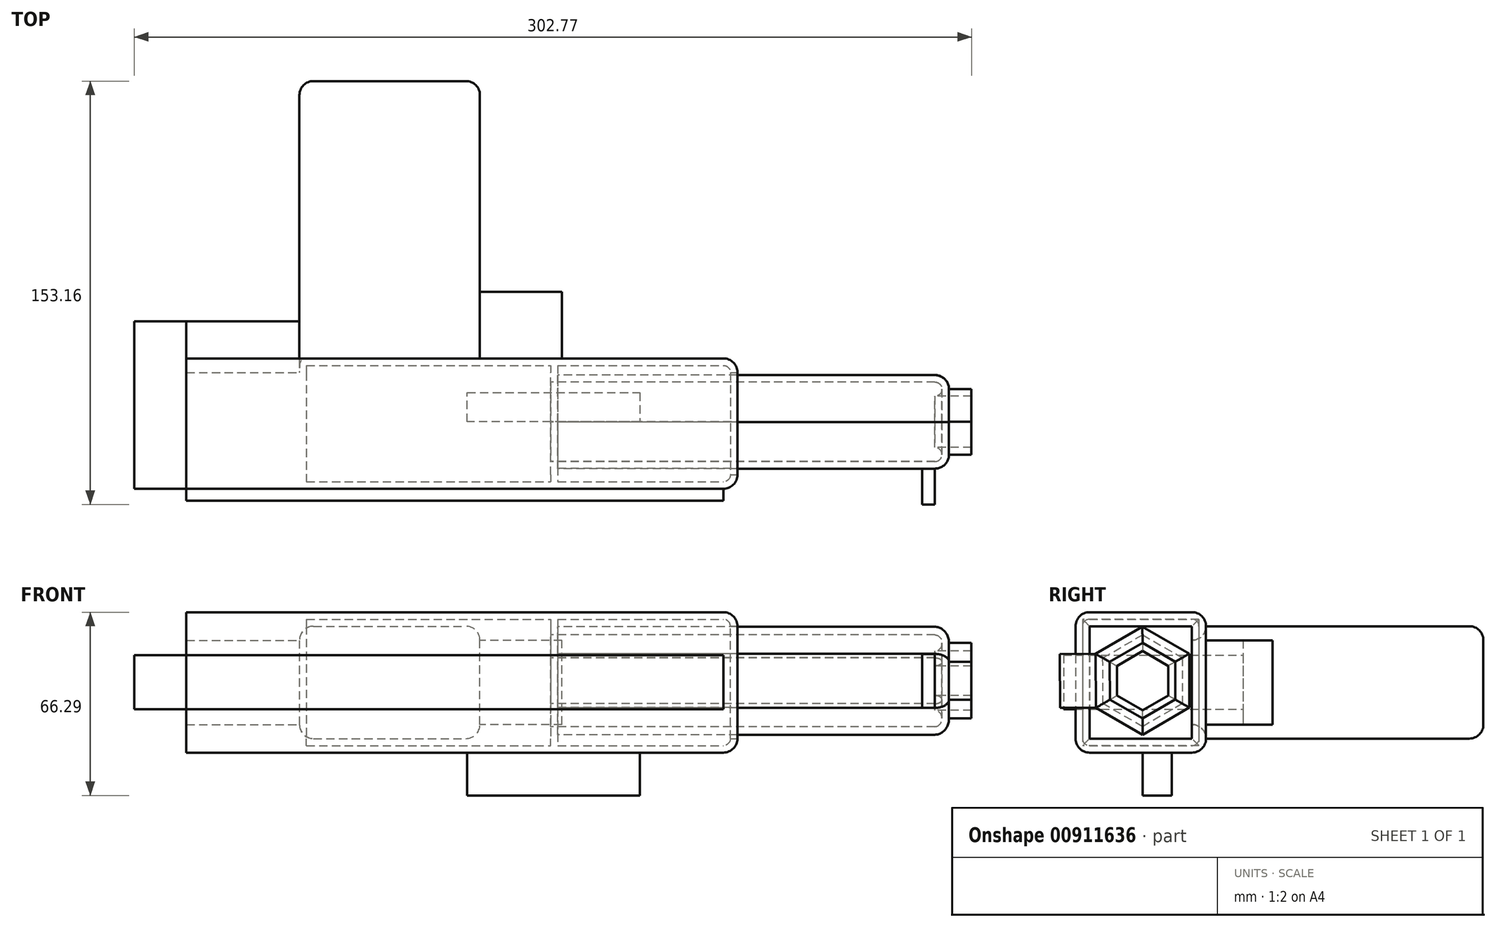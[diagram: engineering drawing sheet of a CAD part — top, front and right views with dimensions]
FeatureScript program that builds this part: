
annotation { "Feature Type Name" : "Feature", "Feature Type Description" : "" }
export const myFeature = defineFeature(function(context is Context, id is Id, definition is map)
    precondition{}
    {
        {
            var Q0;
            Q0=qCreatedBy(makeId("Top.planeOp"),FACE);
            var sketch = newSketch(context, id + "F0", { "sketchPlane" : qUnion([Q0])});
            skLineSegment(sketch, "E0.bottom", {"start": v(-32.17, 22.95) * mm, "end": v(35.3, 22.95) * mm});
            skLineSegment(sketch, "E0.top", {"start": v(-32.17, -24.24) * mm, "end": v(35.3, -24.24) * mm});
            skLineSegment(sketch, "E0.left", {"start": v(-32.17, 22.95) * mm, "end": v(-32.17, -24.24) * mm});
            skLineSegment(sketch, "E0.right", {"start": v(35.3, 22.95) * mm, "end": v(35.3, -24.24) * mm});
            skSolve(sketch);
        }
        {
            var Q0;
            Q0=makeQuery(id+"F0.imprint","IMPRINT",FACE,{"disambiguationData":[TD([[makeQuery(id+"F0.imprint","IMPRINT",EDGE,{"derivedFrom":sQuery(id+"F0.wireOp",EDGE,"E0.bottom")}),-1.0]])]});
            extrude(context, id + "F1", {"entities" : qUnion([Q0]), "depth" : 50.8 * mm, "offsetDistance" : 25.4 * mm});
        }
        {
            var Q0;
            Q0=makeQuery(id+"F1.opExtrude","CAP_EDGE",EDGE,{"disambiguationData":[OSD([sQuery(id+"F0.wireOp",EDGE,"E0.right")])],"isStart":false});
            var Q1;
            Q1=makeQuery(id+"F1.opExtrude","SWEPT_EDGE",EDGE,{"disambiguationData":[OSD([sQuery(id+"F0.wireOp",EDGE,"E0.top"),sQuery(id+"F0.wireOp",EDGE,"E0.right")])]});
            var Q2;
            Q2=makeQuery(id+"F1.opExtrude","CAP_EDGE",EDGE,{"disambiguationData":[OSD([sQuery(id+"F0.wireOp",EDGE,"E0.right")])],"isStart":true});
            var Q3;
            Q3=makeQuery(id+"F1.opExtrude","SWEPT_EDGE",EDGE,{"disambiguationData":[OSD([sQuery(id+"F0.wireOp",EDGE,"E0.bottom"),sQuery(id+"F0.wireOp",EDGE,"E0.right")])]});
            fillet(context, id + "F2", {"entities" : qUnion([Q0, Q1, Q2, Q3]), "radius" : 5.08 * mm, "tangentPropagation" : true, "allowEdgeOverflow" : false});
        }
        {
            var Q0;
            Q0=makeQuery(id+"F1.opExtrude","SWEPT_FACE",FACE,{"disambiguationData":[OSD([sQuery(id+"F0.wireOp",EDGE,"E0.right")])]});
            shell(context, id + "F3", {"entities" : qUnion([Q0]), "thickness" : 2.54 * mm});
        }
        {
            var Q0;
            Q0=makeQuery(id+"F1.opExtrude","CAP_EDGE",EDGE,{"disambiguationData":[OSD([sQuery(id+"F0.wireOp",EDGE,"E0.top")])],"isStart":true});
            var Q1;
            Q1=makeQuery(id+"F1.opExtrude","CAP_EDGE",EDGE,{"disambiguationData":[OSD([sQuery(id+"F0.wireOp",EDGE,"E0.bottom")])],"isStart":true});
            var Q2;
            Q2=makeQuery(id+"F1.opExtrude","CAP_EDGE",EDGE,{"disambiguationData":[OSD([sQuery(id+"F0.wireOp",EDGE,"E0.bottom")])],"isStart":false});
            var Q3;
            Q3=makeQuery(id+"F1.opExtrude","CAP_EDGE",EDGE,{"disambiguationData":[OSD([sQuery(id+"F0.wireOp",EDGE,"E0.top")])],"isStart":false});
            fillet(context, id + "F4", {"entities" : qUnion([Q0, Q1, Q2, Q3]), "radius" : 5.08 * mm, "tangentPropagation" : true, "allowEdgeOverflow" : false});
        }
        {
            var Q0;
            Q0=makeQuery(id+"F3.opShell","OFFSET_FACE",FACE,{"disambiguationData":[OSD([sQuery(id+"F0.wireOp",EDGE,"E0.left")])]});
            var sketch = newSketch(context, id + "F5", { "sketchPlane" : qUnion([Q0])});
            skCircle(sketch, "E1.cCircle", {"center": v(0, 26) * mm, "radius": 16.9 * mm, "construction": true});
            skLineSegment(sketch, "E1.0", {"start": v(-16.93, 35.73) * mm, "end": v(-0.04, 45.53) * mm});
            skLineSegment(sketch, "E1.1", {"start": v(-0.04, 45.53) * mm, "end": v(16.89, 35.8) * mm});
            skLineSegment(sketch, "E1.2", {"start": v(16.89, 35.8) * mm, "end": v(16.93, 16.28) * mm});
            skLineSegment(sketch, "E1.3", {"start": v(16.93, 16.28) * mm, "end": v(0.04, 6.48) * mm});
            skLineSegment(sketch, "E1.4", {"start": v(0.04, 6.48) * mm, "end": v(-16.89, 16.2) * mm});
            skLineSegment(sketch, "E1.5", {"start": v(-16.89, 16.2) * mm, "end": v(-16.93, 35.73) * mm});
            skPoint(sketch, "E1.0.midPoint", {"position": v(-8.48, 40.63) * mm});
            skSolve(sketch);
        }
        {
            var Q0;
            Q0 = qSketchRegion(id + "F5", true);
            extrude(context, id + "F6", {"entities" : qUnion([Q0]), "operationType" : NewBodyOperationType.ADD, "depth" : 141.48 * mm, "offsetDistance" : 25.4 * mm});
        }
        {
            var Q0;
            Q0=makeQuery(id+"F6.opExtrude","CAP_EDGE",EDGE,{"disambiguationData":[OSD([sQuery(id+"F5.wireOp",EDGE,"E1.5")])],"isStart":false});
            var Q1;
            Q1=makeQuery(id+"F6.opExtrude","CAP_EDGE",EDGE,{"disambiguationData":[OSD([sQuery(id+"F5.wireOp",EDGE,"E1.2")])],"isStart":false});
            var Q2;
            Q2=makeQuery(id+"F6.opExtrude","CAP_EDGE",EDGE,{"disambiguationData":[OSD([sQuery(id+"F5.wireOp",EDGE,"E1.4")])],"isStart":false});
            var Q3;
            Q3=makeQuery(id+"F6.opExtrude","CAP_EDGE",EDGE,{"disambiguationData":[OSD([sQuery(id+"F5.wireOp",EDGE,"E1.0")])],"isStart":false});
            var Q4;
            Q4=makeQuery(id+"F6.opExtrude","CAP_EDGE",EDGE,{"disambiguationData":[OSD([sQuery(id+"F5.wireOp",EDGE,"E1.1")])],"isStart":false});
            var Q5;
            Q5=makeQuery(id+"F6.opExtrude","CAP_EDGE",EDGE,{"disambiguationData":[OSD([sQuery(id+"F5.wireOp",EDGE,"E1.3")])],"isStart":false});
            fillet(context, id + "F7", {"entities" : qUnion([Q0, Q1, Q2, Q3, Q4, Q5]), "radius" : 5.08 * mm, "tangentPropagation" : true, "allowEdgeOverflow" : false});
        }
        {
            var Q0;
            Q0=makeQuery(id+"F6.opExtrude","CAP_FACE",FACE,{"disambiguationData":[OSD([sQuery(id+"F5.wireOp",EDGE,"E1.0"),sQuery(id+"F5.wireOp",EDGE,"E1.1"),sQuery(id+"F5.wireOp",EDGE,"E1.2"),sQuery(id+"F5.wireOp",EDGE,"E1.3"),sQuery(id+"F5.wireOp",EDGE,"E1.4"),sQuery(id+"F5.wireOp",EDGE,"E1.5")])],"isStart":false});
            extrude(context, id + "F8", {"entities" : qUnion([Q0]), "operationType" : NewBodyOperationType.ADD, "depth" : 8.13 * mm, "offsetDistance" : 25.4 * mm});
        }
        {
            var Q0;
            Q0=makeQuery(id+"F1.opExtrude","SWEPT_FACE",FACE,{"disambiguationData":[OSD([sQuery(id+"F0.wireOp",EDGE,"E0.left")])]});
            extrude(context, id + "F9", {"entities" : qUnion([Q0]), "operationType" : NewBodyOperationType.ADD, "depth" : 90.93 * mm, "offsetDistance" : 25.4 * mm});
        }
        {
            var Q0;
            Q0=makeQuery(id+"F8.opExtrude","CAP_FACE",FACE,{"disambiguationData":[OSD([sQuery(id+"F5.wireOp",EDGE,"E1.0"),sQuery(id+"F5.wireOp",EDGE,"E1.1"),sQuery(id+"F5.wireOp",EDGE,"E1.2"),sQuery(id+"F5.wireOp",EDGE,"E1.3"),sQuery(id+"F5.wireOp",EDGE,"E1.4"),sQuery(id+"F5.wireOp",EDGE,"E1.5")])],"isStart":false});
            shell(context, id + "F10", {"entities" : qUnion([Q0]), "thickness" : 2.54 * mm});
        }
        {
            var Q0;
            {var subQ0=sQuery(id+"F0.wireOp",EDGE,"E0.left");var subQ1=sQuery(id+"F0.wireOp",EDGE,"E0.bottom");Q0=makeQuery(id+"F9.boolean.opBoolean","MERGE",FACE,{"derivedFrom":[makeQuery(id+"F1.opExtrude","SWEPT_FACE",FACE,{"disambiguationData":[OSD([subQ1])]}),makeQuery(id+"F9.opExtrude","SWEPT_FACE",FACE,{"disambiguationData":[OSD([subQ1,subQ0]),TDD([makeQuery(id+"F1.opExtrude","SWEPT_EDGE",EDGE,{"disambiguationData":[OSD([subQ1,subQ0])]})])]})]});}
            var sketch = newSketch(context, id + "F11", { "sketchPlane" : qUnion([Q0])});
            skLineSegment(sketch, "E2", {"start": v(57.84, 5.08) * mm, "end": v(57.84, 45.72) * mm});
            skSolve(sketch);
        }
        {
            var Q0;
            {var subQ0=sQuery(id+"F11.wireOp",EDGE,"E2");Q0=makeQuery(id+"F11.imprint","IMPRINT",FACE,{"disambiguationData":[TD([[makeQuery(id+"F11.imprint","IMPRINT",EDGE,{"derivedFrom":subQ0}),-1.0]])]});}
            extrude(context, id + "F12", {"entities" : qUnion([Q0]), "operationType" : NewBodyOperationType.ADD, "depth" : 100.33 * mm, "offsetDistance" : 25.4 * mm});
        }
        {
            var Q0;
            {var subQ0=sQuery(id+"F11.wireOp",EDGE,"E2");var subQ1=sQuery(id+"F0.wireOp",EDGE,"E0.bottom");var subQ2=makeQuery(id+"F1.opExtrude","SWEPT_FACE",FACE,{"disambiguationData":[OSD([subQ1])]});var subQ3=sQuery(id+"F0.wireOp",EDGE,"E0.left");var subQ4=makeQuery(id+"F1.opExtrude","CAP_EDGE",EDGE,{"disambiguationData":[OSD([subQ1])],"isStart":true});Q0=makeQuery(id+"F12.opExtrude","SWEPT_EDGE",EDGE,{"disambiguationData":[OSD([subQ1,subQ3,subQ0]),TDD([makeQuery(id+"F11.imprint","INTERSECT",VERTEX,{"derivedFrom":[makeQuery(id+"F9.boolean.opBoolean","MERGE",EDGE,{"derivedFrom":[makeQuery(id+"F4.opFillet","BLEND_EDGE",EDGE,{"blendedFrom":[subQ4,subQ2],"blendedInto":[subQ2]}),makeQuery(id+"F9.opExtrude","SWEPT_EDGE",EDGE,{"disambiguationData":[OSD([subQ1,subQ3]),TDD([makeQuery(id+"F4.opFillet","BLEND_VERTEX",VERTEX,{"blendedFrom":[subQ4,makeQuery(id+"F1.opExtrude","SWEPT_FACE",FACE,{"disambiguationData":[OSD([subQ3])]}),subQ2],"blendedInto":[makeQuery(id+"F1.opExtrude","SWEPT_FACE",FACE,{"disambiguationData":[OSD([subQ3])]}),subQ2]})])]})]}),subQ0]})])]});}
            var Q1;
            {var subQ0=sQuery(id+"F11.wireOp",EDGE,"E2");var subQ1=sQuery(id+"F0.wireOp",EDGE,"E0.bottom");var subQ2=makeQuery(id+"F1.opExtrude","SWEPT_FACE",FACE,{"disambiguationData":[OSD([subQ1])]});var subQ3=sQuery(id+"F0.wireOp",EDGE,"E0.left");var subQ4=makeQuery(id+"F1.opExtrude","CAP_EDGE",EDGE,{"disambiguationData":[OSD([subQ1])],"isStart":false});Q1=makeQuery(id+"F12.opExtrude","SWEPT_EDGE",EDGE,{"disambiguationData":[OSD([subQ1,subQ3,subQ0]),TDD([makeQuery(id+"F11.imprint","INTERSECT",VERTEX,{"derivedFrom":[makeQuery(id+"F9.boolean.opBoolean","MERGE",EDGE,{"derivedFrom":[makeQuery(id+"F4.opFillet","BLEND_EDGE",EDGE,{"blendedFrom":[subQ4,subQ2],"blendedInto":[subQ2]}),makeQuery(id+"F9.opExtrude","SWEPT_EDGE",EDGE,{"disambiguationData":[OSD([subQ1,subQ3]),TDD([makeQuery(id+"F4.opFillet","BLEND_VERTEX",VERTEX,{"blendedFrom":[subQ4,makeQuery(id+"F1.opExtrude","SWEPT_FACE",FACE,{"disambiguationData":[OSD([subQ3])]}),subQ2],"blendedInto":[makeQuery(id+"F1.opExtrude","SWEPT_FACE",FACE,{"disambiguationData":[OSD([subQ3])]}),subQ2]})])]})]}),subQ0]})])]});}
            var Q2;
            {var subQ0=sQuery(id+"F0.wireOp",EDGE,"E0.bottom");var subQ1=makeQuery(id+"F1.opExtrude","SWEPT_FACE",FACE,{"disambiguationData":[OSD([subQ0])]});var subQ2=sQuery(id+"F0.wireOp",EDGE,"E0.left");var subQ3=makeQuery(id+"F1.opExtrude","CAP_EDGE",EDGE,{"disambiguationData":[OSD([subQ0])],"isStart":false});Q2=makeQuery(id+"F12.opExtrude","SWEPT_EDGE",EDGE,{"disambiguationData":[OSD([subQ0,subQ2]),TDD([makeQuery(id+"F11.imprint","INTERSECT",VERTEX,{"derivedFrom":[makeQuery(id+"F9.opExtrude","CAP_EDGE",EDGE,{"disambiguationData":[OSD([subQ0,subQ2]),TDD([makeQuery(id+"F1.opExtrude","SWEPT_EDGE",EDGE,{"disambiguationData":[OSD([subQ0,subQ2])]})])],"isStart":false}),makeQuery(id+"F9.boolean.opBoolean","MERGE",EDGE,{"derivedFrom":[makeQuery(id+"F4.opFillet","BLEND_EDGE",EDGE,{"blendedFrom":[subQ3,subQ1],"blendedInto":[subQ1]}),makeQuery(id+"F9.opExtrude","SWEPT_EDGE",EDGE,{"disambiguationData":[OSD([subQ0,subQ2]),TDD([makeQuery(id+"F4.opFillet","BLEND_VERTEX",VERTEX,{"blendedFrom":[subQ3,makeQuery(id+"F1.opExtrude","SWEPT_FACE",FACE,{"disambiguationData":[OSD([subQ2])]}),subQ1],"blendedInto":[makeQuery(id+"F1.opExtrude","SWEPT_FACE",FACE,{"disambiguationData":[OSD([subQ2])]}),subQ1]})])]})]})]})])]});}
            var Q3;
            {var subQ0=sQuery(id+"F0.wireOp",EDGE,"E0.bottom");var subQ1=makeQuery(id+"F1.opExtrude","SWEPT_FACE",FACE,{"disambiguationData":[OSD([subQ0])]});var subQ2=sQuery(id+"F0.wireOp",EDGE,"E0.left");var subQ3=makeQuery(id+"F1.opExtrude","CAP_EDGE",EDGE,{"disambiguationData":[OSD([subQ0])],"isStart":true});Q3=makeQuery(id+"F12.opExtrude","SWEPT_EDGE",EDGE,{"disambiguationData":[OSD([subQ0,subQ2]),TDD([makeQuery(id+"F11.imprint","INTERSECT",VERTEX,{"derivedFrom":[makeQuery(id+"F9.opExtrude","CAP_EDGE",EDGE,{"disambiguationData":[OSD([subQ0,subQ2]),TDD([makeQuery(id+"F1.opExtrude","SWEPT_EDGE",EDGE,{"disambiguationData":[OSD([subQ0,subQ2])]})])],"isStart":false}),makeQuery(id+"F9.boolean.opBoolean","MERGE",EDGE,{"derivedFrom":[makeQuery(id+"F4.opFillet","BLEND_EDGE",EDGE,{"blendedFrom":[subQ3,subQ1],"blendedInto":[subQ1]}),makeQuery(id+"F9.opExtrude","SWEPT_EDGE",EDGE,{"disambiguationData":[OSD([subQ0,subQ2]),TDD([makeQuery(id+"F4.opFillet","BLEND_VERTEX",VERTEX,{"blendedFrom":[subQ3,makeQuery(id+"F1.opExtrude","SWEPT_FACE",FACE,{"disambiguationData":[OSD([subQ2])]}),subQ1],"blendedInto":[makeQuery(id+"F1.opExtrude","SWEPT_FACE",FACE,{"disambiguationData":[OSD([subQ2])]}),subQ1]})])]})]})]})])]});}
            var Q4;
            {var subQ0=sQuery(id+"F0.wireOp",EDGE,"E0.bottom");var subQ1=makeQuery(id+"F1.opExtrude","SWEPT_FACE",FACE,{"disambiguationData":[OSD([subQ0])]});var subQ2=sQuery(id+"F0.wireOp",EDGE,"E0.left");var subQ3=makeQuery(id+"F1.opExtrude","CAP_EDGE",EDGE,{"disambiguationData":[OSD([subQ0])],"isStart":true});var subQ4=makeQuery(id+"F9.boolean.opBoolean","MERGE",EDGE,{"derivedFrom":[makeQuery(id+"F4.opFillet","BLEND_EDGE",EDGE,{"blendedFrom":[subQ3,subQ1],"blendedInto":[subQ1]}),makeQuery(id+"F9.opExtrude","SWEPT_EDGE",EDGE,{"disambiguationData":[OSD([subQ0,subQ2]),TDD([makeQuery(id+"F4.opFillet","BLEND_VERTEX",VERTEX,{"blendedFrom":[subQ3,makeQuery(id+"F1.opExtrude","SWEPT_FACE",FACE,{"disambiguationData":[OSD([subQ2])]}),subQ1],"blendedInto":[makeQuery(id+"F1.opExtrude","SWEPT_FACE",FACE,{"disambiguationData":[OSD([subQ2])]}),subQ1]})])]})]});Q4=makeQuery(id+"F12.opExtrude","CAP_EDGE",EDGE,{"disambiguationData":[OSD([subQ0,subQ2]),TDD([makeQuery(id+"F11.imprint","IMPRINT",EDGE,{"disambiguationData":[TD([[makeQuery(id+"F11.imprint","INTERSECT",VERTEX,{"derivedFrom":[subQ4,sQuery(id+"F11.wireOp",EDGE,"E2")]}),-1.0]])],"derivedFrom":subQ4})])],"isStart":false});}
            var Q5;
            {var subQ0=sQuery(id+"F0.wireOp",EDGE,"E0.bottom");var subQ1=makeQuery(id+"F1.opExtrude","SWEPT_FACE",FACE,{"disambiguationData":[OSD([subQ0])]});var subQ2=sQuery(id+"F0.wireOp",EDGE,"E0.left");var subQ3=makeQuery(id+"F1.opExtrude","CAP_EDGE",EDGE,{"disambiguationData":[OSD([subQ0])],"isStart":false});var subQ4=makeQuery(id+"F9.boolean.opBoolean","MERGE",EDGE,{"derivedFrom":[makeQuery(id+"F4.opFillet","BLEND_EDGE",EDGE,{"blendedFrom":[subQ3,subQ1],"blendedInto":[subQ1]}),makeQuery(id+"F9.opExtrude","SWEPT_EDGE",EDGE,{"disambiguationData":[OSD([subQ0,subQ2]),TDD([makeQuery(id+"F4.opFillet","BLEND_VERTEX",VERTEX,{"blendedFrom":[subQ3,makeQuery(id+"F1.opExtrude","SWEPT_FACE",FACE,{"disambiguationData":[OSD([subQ2])]}),subQ1],"blendedInto":[makeQuery(id+"F1.opExtrude","SWEPT_FACE",FACE,{"disambiguationData":[OSD([subQ2])]}),subQ1]})])]})]});Q5=makeQuery(id+"F12.opExtrude","CAP_EDGE",EDGE,{"disambiguationData":[OSD([subQ0,subQ2]),TDD([makeQuery(id+"F11.imprint","IMPRINT",EDGE,{"disambiguationData":[TD([[makeQuery(id+"F11.imprint","INTERSECT",VERTEX,{"derivedFrom":[subQ4,sQuery(id+"F11.wireOp",EDGE,"E2")]}),1.0]])],"derivedFrom":subQ4})])],"isStart":false});}
            var Q6;
            {var subQ0=sQuery(id+"F0.wireOp",EDGE,"E0.left");var subQ1=sQuery(id+"F0.wireOp",EDGE,"E0.bottom");Q6=makeQuery(id+"F12.opExtrude","CAP_EDGE",EDGE,{"disambiguationData":[OSD([subQ1,subQ0]),TDD([makeQuery(id+"F11.imprint","IMPRINT",EDGE,{"derivedFrom":makeQuery(id+"F9.opExtrude","CAP_EDGE",EDGE,{"disambiguationData":[OSD([subQ1,subQ0]),TDD([makeQuery(id+"F1.opExtrude","SWEPT_EDGE",EDGE,{"disambiguationData":[OSD([subQ1,subQ0])]})])],"isStart":false})})])],"isStart":false});}
            var Q7;
            Q7=makeQuery(id+"F12.opExtrude","CAP_EDGE",EDGE,{"disambiguationData":[OSD([sQuery(id+"F11.wireOp",EDGE,"E2")])],"isStart":false});
            fillet(context, id + "F13", {"entities" : qUnion([Q0, Q1, Q2, Q3, Q4, Q5, Q6, Q7]), "radius" : 5.08 * mm, "tangentPropagation" : true, "allowEdgeOverflow" : false});
        }
        {
            var Q0;
            {var subQ0=sQuery(id+"F0.wireOp",EDGE,"E0.left");var subQ1=sQuery(id+"F0.wireOp",EDGE,"E0.bottom");Q0=makeQuery(id+"F12.boolean.opBoolean","MERGE",FACE,{"derivedFrom":[makeQuery(id+"F9.opExtrude","CAP_FACE",FACE,{"disambiguationData":[OSD([subQ0])],"isStart":false}),makeQuery(id+"F12.opExtrude","SWEPT_FACE",FACE,{"disambiguationData":[OSD([subQ1,subQ0]),TDD([makeQuery(id+"F11.imprint","IMPRINT",EDGE,{"derivedFrom":makeQuery(id+"F9.opExtrude","CAP_EDGE",EDGE,{"disambiguationData":[OSD([subQ1,subQ0]),TDD([makeQuery(id+"F1.opExtrude","SWEPT_EDGE",EDGE,{"disambiguationData":[OSD([subQ1,subQ0])]})])],"isStart":false})})])]})]});}
            var sketch = newSketch(context, id + "F14", { "sketchPlane" : qUnion([Q0])});
            skLineSegment(sketch, "E3", {"start": v(-17.87, 40.64) * mm, "end": v(-17.87, 10.16) * mm});
            skSolve(sketch);
        }
        {
            var Q0;
            Q0=makeQuery(id+"F14.imprint","IMPRINT",FACE,{"disambiguationData":[TD([[makeQuery(id+"F14.imprint","IMPRINT",EDGE,{"derivedFrom":sQuery(id+"F14.wireOp",EDGE,"E3")}),1.0]])]});
            extrude(context, id + "F15", {"entities" : qUnion([Q0]), "operationType" : NewBodyOperationType.ADD, "depth" : 40.9 * mm, "offsetDistance" : 25.4 * mm});
        }
        {
            var Q0;
            {var subQ0=sQuery(id+"F0.wireOp",EDGE,"E0.left");var subQ1=makeQuery(id+"F1.opExtrude","CAP_EDGE",EDGE,{"disambiguationData":[OSD([subQ0])],"isStart":true});Q0=makeQuery(id+"F15.boolean.opBoolean","MERGE",FACE,{"derivedFrom":[makeQuery(id+"F9.boolean.opBoolean","MERGE",FACE,{"derivedFrom":[makeQuery(id+"F1.opExtrude","CAP_FACE",FACE,{"disambiguationData":[OSD([sQuery(id+"F0.wireOp",EDGE,"E0.bottom"),sQuery(id+"F0.wireOp",EDGE,"E0.top"),subQ0,sQuery(id+"F0.wireOp",EDGE,"E0.right")])],"isStart":true}),makeQuery(id+"F9.opExtrude","SWEPT_FACE",FACE,{"disambiguationData":[OSD([subQ0]),TDD([subQ1])]})]}),makeQuery(id+"F15.opExtrude","SWEPT_FACE",FACE,{"disambiguationData":[OSD([subQ0]),TDD([makeQuery(id+"F14.imprint","IMPRINT",EDGE,{"derivedFrom":makeQuery(id+"F9.opExtrude","CAP_EDGE",EDGE,{"disambiguationData":[OSD([subQ0]),TDD([subQ1])],"isStart":false})})])]})]});}
            var sketch = newSketch(context, id + "F16", { "sketchPlane" : qUnion([Q0])});
            skLineSegment(sketch, "E4", {"start": v(0, 0) * mm, "end": v(-62.4, 0) * mm});
            skLineSegment(sketch, "E5", {"start": v(-62.4, 0) * mm, "end": v(-62.4, -10.55) * mm});
            skLineSegment(sketch, "E6", {"start": v(-62.4, -10.55) * mm, "end": v(0, -10.55) * mm});
            skLineSegment(sketch, "E7", {"start": v(0, -10.55) * mm, "end": v(0, 0) * mm});
            skSolve(sketch);
        }
        {
            var Q0;
            Q0=makeQuery(id+"F16.imprint","IMPRINT",FACE,{"disambiguationData":[TD([[makeQuery(id+"F16.imprint","IMPRINT",EDGE,{"derivedFrom":sQuery(id+"F16.wireOp",EDGE,"E4")}),1.0]])]});
            extrude(context, id + "F17", {"entities" : qUnion([Q0]), "operationType" : NewBodyOperationType.ADD, "depth" : 15.5 * mm, "offsetDistance" : 25.4 * mm});
        }
        {
            var Q0;
            Q0=makeQuery(id+"F15.opExtrude","CAP_FACE",FACE,{"disambiguationData":[OSD([sQuery(id+"F0.wireOp",EDGE,"E0.bottom"),sQuery(id+"F0.wireOp",EDGE,"E0.top"),sQuery(id+"F0.wireOp",EDGE,"E0.left"),sQuery(id+"F14.wireOp",EDGE,"E3")])],"isStart":false});
            var sketch = newSketch(context, id + "F18", { "sketchPlane" : qUnion([Q0])});
            skLineSegment(sketch, "E8", {"start": v(24.24, 35.3) * mm, "end": v(-17.87, 35.3) * mm});
            skLineSegment(sketch, "E9", {"start": v(24.24, 15.64) * mm, "end": v(-17.87, 15.64) * mm});
            skSolve(sketch);
        }
        {
            var Q0;
            {var subQ0=sQuery(id+"F18.wireOp",EDGE,"E8");Q0=makeQuery(id+"F18.imprint","IMPRINT",FACE,{"disambiguationData":[TD([[makeQuery(id+"F18.imprint","IMPRINT",EDGE,{"derivedFrom":subQ0}),1.0]])]});}
            extrude(context, id + "F19", {"entities" : qUnion([Q0]), "operationType" : NewBodyOperationType.ADD, "depth" : 18.8 * mm, "offsetDistance" : 25.4 * mm});
        }
        {
            var Q0;
            {var subQ0=sQuery(id+"F0.wireOp",EDGE,"E0.left");var subQ1=sQuery(id+"F0.wireOp",EDGE,"E0.top");var subQ2=makeQuery(id+"F1.opExtrude","SWEPT_EDGE",EDGE,{"disambiguationData":[OSD([subQ1,subQ0])]});Q0=makeQuery(id+"F19.boolean.opBoolean","MERGE",FACE,{"derivedFrom":[makeQuery(id+"F15.boolean.opBoolean","MERGE",FACE,{"derivedFrom":[makeQuery(id+"F9.boolean.opBoolean","MERGE",FACE,{"derivedFrom":[makeQuery(id+"F1.opExtrude","SWEPT_FACE",FACE,{"disambiguationData":[OSD([subQ1])]}),makeQuery(id+"F9.opExtrude","SWEPT_FACE",FACE,{"disambiguationData":[OSD([subQ1,subQ0]),TDD([subQ2])]})]}),makeQuery(id+"F15.opExtrude","SWEPT_FACE",FACE,{"disambiguationData":[OSD([subQ1,subQ0]),TDD([makeQuery(id+"F14.imprint","IMPRINT",EDGE,{"derivedFrom":makeQuery(id+"F9.opExtrude","CAP_EDGE",EDGE,{"disambiguationData":[OSD([subQ1,subQ0]),TDD([subQ2])],"isStart":false})})])]})]}),makeQuery(id+"F19.opExtrude","SWEPT_FACE",FACE,{"disambiguationData":[OSD([subQ1,subQ0])]})]});}
            var sketch = newSketch(context, id + "F20", { "sketchPlane" : qUnion([Q0])});
            skLineSegment(sketch, "E10", {"start": v(-164, 35.3) * mm, "end": v(30.22, 35.3) * mm});
            skLineSegment(sketch, "E11", {"start": v(-164, 15.64) * mm, "end": v(30.22, 15.64) * mm});
            skLineSegment(sketch, "E12", {"start": v(-164, 35.3) * mm, "end": v(-164, 15.64) * mm});
            skSolve(sketch);
        }
        {
            var Q0;
            {var subQ0=sQuery(id+"F20.wireOp",EDGE,"E10");Q0=makeQuery(id+"F20.imprint","IMPRINT",FACE,{"disambiguationData":[TD([[makeQuery(id+"F20.imprint","IMPRINT",EDGE,{"derivedFrom":subQ0}),-1.0]])]});}
            extrude(context, id + "F21", {"entities" : qUnion([Q0]), "operationType" : NewBodyOperationType.ADD, "depth" : 4.32 * mm, "offsetDistance" : 25.4 * mm});
        }
        {
            var Q0;
            Q0=makeQuery(id+"F12.opExtrude","SWEPT_FACE",FACE,{"disambiguationData":[OSD([sQuery(id+"F11.wireOp",EDGE,"E2")])]});
            var sketch = newSketch(context, id + "F22", { "sketchPlane" : qUnion([Q0])});
            skLineSegment(sketch, "E13", {"start": v(46.97, 10.16) * mm, "end": v(46.97, 40.64) * mm});
            skSolve(sketch);
        }
        {
            var Q0;
            {var subQ0=sQuery(id+"F22.wireOp",EDGE,"E13");Q0=makeQuery(id+"F22.imprint","IMPRINT",FACE,{"disambiguationData":[TD([[makeQuery(id+"F22.imprint","IMPRINT",EDGE,{"derivedFrom":subQ0}),1.0]])]});}
            extrude(context, id + "F23", {"entities" : qUnion([Q0]), "operationType" : NewBodyOperationType.ADD, "depth" : 29.72 * mm, "offsetDistance" : 25.4 * mm});
        }
        {
            var Q0;
            {var subQ0=sQuery(id+"F14.wireOp",EDGE,"E3");Q0=makeQuery(id+"F19.boolean.opBoolean","MERGE",FACE,{"derivedFrom":[makeQuery(id+"F15.opExtrude","SWEPT_FACE",FACE,{"disambiguationData":[OSD([subQ0])]}),makeQuery(id+"F19.opExtrude","SWEPT_FACE",FACE,{"disambiguationData":[OSD([subQ0])]})]});}
            extrude(context, id + "F24", {"entities" : qUnion([Q0]), "operationType" : NewBodyOperationType.ADD, "depth" : 18.54 * mm, "offsetDistance" : 25.4 * mm});
        }
        {
            var Q0;
            {var subQ0=sQuery(id+"F11.wireOp",EDGE,"E2");var subQ1=sQuery(id+"F0.wireOp",EDGE,"E0.bottom");var subQ2=makeQuery(id+"F1.opExtrude","SWEPT_FACE",FACE,{"disambiguationData":[OSD([subQ1])]});var subQ3=sQuery(id+"F0.wireOp",EDGE,"E0.left");var subQ4=makeQuery(id+"F1.opExtrude","CAP_EDGE",EDGE,{"disambiguationData":[OSD([subQ1])],"isStart":true});var subQ5=makeQuery(id+"F13.opFillet","BLEND_EDGE",EDGE,{"blendedFrom":[makeQuery(id+"F12.opExtrude","SWEPT_EDGE",EDGE,{"disambiguationData":[OSD([subQ1,subQ3,subQ0]),TDD([makeQuery(id+"F11.imprint","INTERSECT",VERTEX,{"derivedFrom":[makeQuery(id+"F9.boolean.opBoolean","MERGE",EDGE,{"derivedFrom":[makeQuery(id+"F4.opFillet","BLEND_EDGE",EDGE,{"blendedFrom":[subQ4,subQ2],"blendedInto":[subQ2]}),makeQuery(id+"F9.opExtrude","SWEPT_EDGE",EDGE,{"disambiguationData":[OSD([subQ1,subQ3]),TDD([makeQuery(id+"F4.opFillet","BLEND_VERTEX",VERTEX,{"blendedFrom":[subQ4,makeQuery(id+"F1.opExtrude","SWEPT_FACE",FACE,{"disambiguationData":[OSD([subQ3])]}),subQ2],"blendedInto":[makeQuery(id+"F1.opExtrude","SWEPT_FACE",FACE,{"disambiguationData":[OSD([subQ3])]}),subQ2]})])]})]}),subQ0]})])]}),makeQuery(id+"F12.opExtrude","SWEPT_FACE",FACE,{"disambiguationData":[OSD([subQ0])]})],"blendedInto":[makeQuery(id+"F12.opExtrude","SWEPT_FACE",FACE,{"disambiguationData":[OSD([subQ0])]})]});Q0=makeQuery(id+"F23.opExtrude","SWEPT_FACE",FACE,{"disambiguationData":[OSD([subQ1,subQ3,subQ0]),TDD([makeQuery(id+"F22.imprint","IMPRINT",EDGE,{"disambiguationData":[TD([[makeQuery(id+"F22.imprint","INTERSECT",VERTEX,{"derivedFrom":[subQ5,makeQuery(id+"F12.opExtrude","CAP_EDGE",EDGE,{"disambiguationData":[OSD([subQ0])],"isStart":true})]}),-1.0]])],"derivedFrom":subQ5})])]});}
            extrude(context, id + "F25", {"entities" : qUnion([Q0]), "operationType" : NewBodyOperationType.ADD, "oppositeDirection" : true, "depth" : 30.48 * mm, "offsetDistance" : 25.4 * mm});
        }
        {
            var Q0;
            Q0=makeQuery(id+"F6.opExtrude","SWEPT_FACE",FACE,{"disambiguationData":[OSD([sQuery(id+"F5.wireOp",EDGE,"E1.5")])]});
            var sketch = newSketch(context, id + "F26", { "sketchPlane" : qUnion([Q0])});
            skLineSegment(sketch, "E14", {"start": v(102.18, 16.24) * mm, "end": v(102.18, 35.76) * mm});
            skSolve(sketch);
        }
        {
            var Q0;
            {var subQ0=sQuery(id+"F26.wireOp",EDGE,"E14");Q0=makeQuery(id+"F26.imprint","IMPRINT",FACE,{"disambiguationData":[TD([[makeQuery(id+"F26.imprint","IMPRINT",EDGE,{"derivedFrom":subQ0}),-1.0]])]});}
            extrude(context, id + "F27", {"entities" : qUnion([Q0]), "operationType" : NewBodyOperationType.ADD, "depth" : 12.95 * mm, "offsetDistance" : 25.4 * mm});
        }
    });
